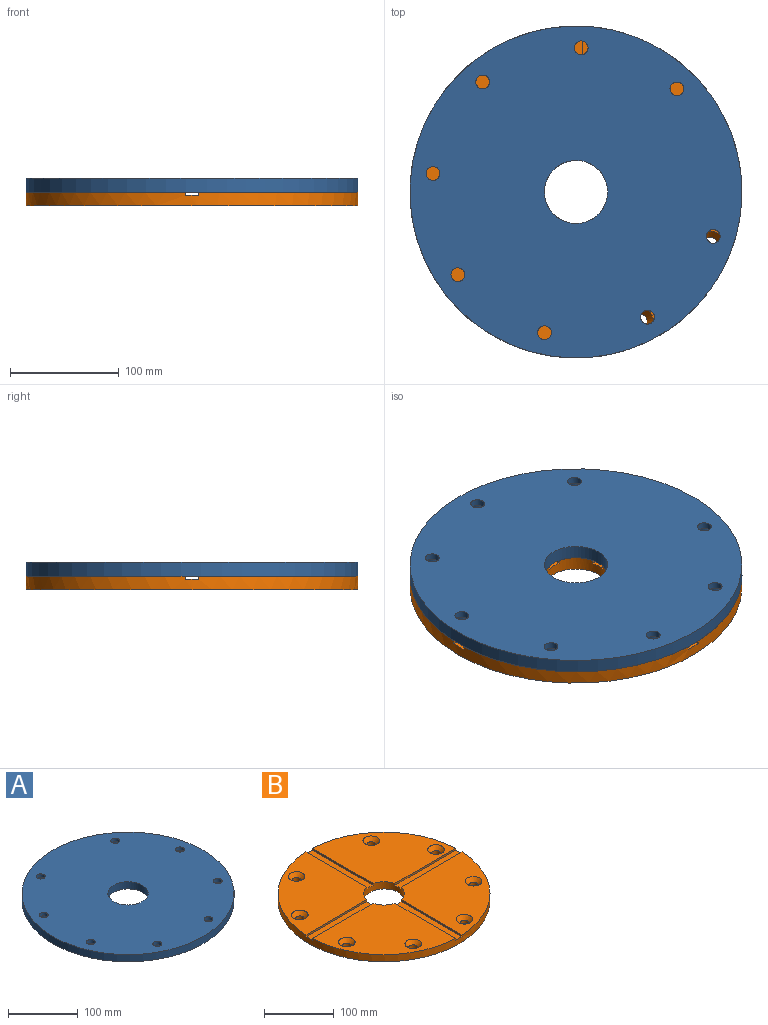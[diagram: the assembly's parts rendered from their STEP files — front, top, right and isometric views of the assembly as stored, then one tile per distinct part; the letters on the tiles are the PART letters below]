
ASSEMBLY  parts=2 mates=1
PART A: 20 faces, bbox 304.8x304.8x12.7 mm
  f0: cylinder r=152.4mm len=304.8mm, axis (0,0,-1), area 12161mm2, adj f1,f2
  f1: plane 304.8x304.8mm, normal (0,0,1), area 69310.4mm2, adj f0,f3,f5,f7,f9,f11,f13,f15
  f2: plane 304.8x304.8mm, normal (0,0,-1), area 66757.2mm2, adj f0,f4,f6,f8,f10,f12,f14,f16
  f3: cylinder r=6.35mm len=12.7mm, axis (0,0,-1), area 251.4mm2, adj f1,f4
  f4: cone r=6.35mm half-angle=41deg, axis (0,0,-1), area 486.5mm2, adj f2,f3
  f5: cylinder r=6.35mm len=12.7mm, axis (0,0,-1), area 251.4mm2, adj f1,f6
  f6: cone r=6.35mm half-angle=41deg, axis (0,0,-1), area 486.5mm2, adj f2,f5
  f7: cylinder r=6.35mm len=12.7mm, axis (0,0,-1), area 251.4mm2, adj f1,f8
  f8: cone r=6.35mm half-angle=41deg, axis (0,0,-1), area 486.5mm2, adj f2,f7
  f9: cylinder r=6.35mm len=12.7mm, axis (0,0,-1), area 251.4mm2, adj f1,f10
  f10: cone r=6.35mm half-angle=41deg, axis (0,0,-1), area 486.5mm2, adj f2,f9
  f11: cylinder r=6.35mm len=12.7mm, axis (0,0,-1), area 251.4mm2, adj f1,f12
  f12: cone r=6.35mm half-angle=41deg, axis (0,0,-1), area 486.5mm2, adj f2,f11
  f13: cylinder r=6.35mm len=12.7mm, axis (0,0,-1), area 251.4mm2, adj f1,f14
  f14: cone r=6.35mm half-angle=41deg, axis (0,0,-1), area 486.5mm2, adj f2,f13
  f15: cylinder r=6.35mm len=12.7mm, axis (0,0,-1), area 251.4mm2, adj f1,f16
  f16: cone r=6.35mm half-angle=41deg, axis (0,0,-1), area 486.5mm2, adj f2,f15
  f17: cylinder r=6.35mm len=12.7mm, axis (0,0,-1), area 251.4mm2, adj f1,f18
  f18: cone r=6.35mm half-angle=41deg, axis (0,0,-1), area 486.5mm2, adj f2,f17
  f19: cylinder r=29mm len=58mm, axis (0,0,-1), area 2314.1mm2, adj f1,f2
PART B: 35 faces, bbox 304.8x304.8x12.7 mm
  f0: plane 124.1x12.7mm, normal (0,0,1), area 1569.6mm2, adj f3,f13,f14,f18
  f1: plane 124.1x12.7mm, normal (0,0,1), area 1569.6mm2, adj f3,f15,f16,f18
  f2: plane 124.1x12.7mm, normal (0,0,1), area 1569.6mm2, adj f3,f9,f10,f18
  f3: cylinder r=152.4mm len=304.8mm, axis (0,0,1), area 11999.6mm2, adj f0,f1,f2,f4,f5,f6,f7,f8
  f4: plane 145.92x145.92mm, normal (0,0,1), area 15119.7mm2, adj f3,f12,f13,f18,f30,f32
  f5: plane 145.92x145.92mm, normal (0,0,1), area 15119.7mm2, adj f3,f14,f15,f18,f26,f28
  f6: plane 145.92x145.92mm, normal (0,0,1), area 15119.7mm2, adj f3,f9,f16,f18,f24,f34
  f7: plane 304.8x304.8mm, normal (0,0,-1), area 69310.4mm2, adj f3,f18,f19,f21,f23,f25,f27,f29
  f8: plane 145.92x145.92mm, normal (0,0,1), area 15119.7mm2, adj f3,f10,f11,f18,f20,f22
  f9: plane 123.97x3.18mm, normal (1,0,0), area 393.6mm2, adj f2,f3,f6,f18
  f10: plane 123.97x3.18mm, normal (-1,0,0), area 393.6mm2, adj f2,f3,f8,f18
  f11: plane 123.97x3.18mm, normal (0,1,0), area 393.6mm2, adj f3,f8,f17,f18
  f12: plane 123.97x3.18mm, normal (0,-1,0), area 393.6mm2, adj f3,f4,f17,f18
  f13: plane 123.97x3.18mm, normal (-1,0,0), area 393.6mm2, adj f0,f3,f4,f18
  f14: plane 123.97x3.18mm, normal (1,0,0), area 393.6mm2, adj f0,f3,f5,f18
  f15: plane 123.97x3.18mm, normal (0,-1,0), area 393.6mm2, adj f1,f3,f5,f18
  f16: plane 123.97x3.18mm, normal (0,1,0), area 393.6mm2, adj f1,f3,f6,f18
  f17: plane 124.1x12.7mm, normal (0,0,1), area 1569.6mm2, adj f3,f11,f12,f18
  f18: cylinder r=29mm len=58mm, axis (0,0,-1), area 2151.5mm2, adj f0,f1,f2,f4,f5,f6,f7,f8
  f19: cylinder r=6.35mm len=12.7mm, axis (0,0,1), area 251.4mm2, adj f7,f20
  f20: cone r=6.35mm half-angle=41deg, axis (0,0,1), area 486.5mm2, adj f8,f19
  f21: cylinder r=6.35mm len=12.7mm, axis (0,0,1), area 251.4mm2, adj f7,f22
  f22: cone r=6.35mm half-angle=41deg, axis (0,0,1), area 486.5mm2, adj f8,f21
  f23: cylinder r=6.35mm len=12.7mm, axis (0,0,1), area 251.4mm2, adj f7,f24
  f24: cone r=6.35mm half-angle=41deg, axis (0,0,1), area 486.5mm2, adj f6,f23
  f25: cylinder r=6.35mm len=12.7mm, axis (0,0,1), area 251.4mm2, adj f7,f26
  f26: cone r=6.35mm half-angle=41deg, axis (0,0,1), area 486.5mm2, adj f5,f25
  f27: cylinder r=6.35mm len=12.7mm, axis (0,0,1), area 251.4mm2, adj f7,f28
  f28: cone r=6.35mm half-angle=41deg, axis (0,0,1), area 486.5mm2, adj f5,f27
  f29: cylinder r=6.35mm len=12.7mm, axis (0,0,1), area 251.4mm2, adj f7,f30
  f30: cone r=6.35mm half-angle=41deg, axis (0,0,1), area 486.5mm2, adj f4,f29
  f31: cylinder r=6.35mm len=12.7mm, axis (0,0,1), area 251.4mm2, adj f7,f32
  f32: cone r=6.35mm half-angle=41deg, axis (0,0,1), area 486.5mm2, adj f4,f31
  f33: cylinder r=6.35mm len=12.7mm, axis (0,0,1), area 251.4mm2, adj f7,f34
  f34: cone r=6.35mm half-angle=41deg, axis (0,0,1), area 486.5mm2, adj f6,f33
PLACE A rot(axis=(0,0,-1),70.9deg) t=(0.01,0.12,12.7)mm
PLACE B rot(axis=(0,0,1),180deg) t=(0.01,0.12,12.7)mm
MATE revolute A.f0 <-> B.f3  axis (0,0,-1) through (0.01,0.12,12.7)mm
